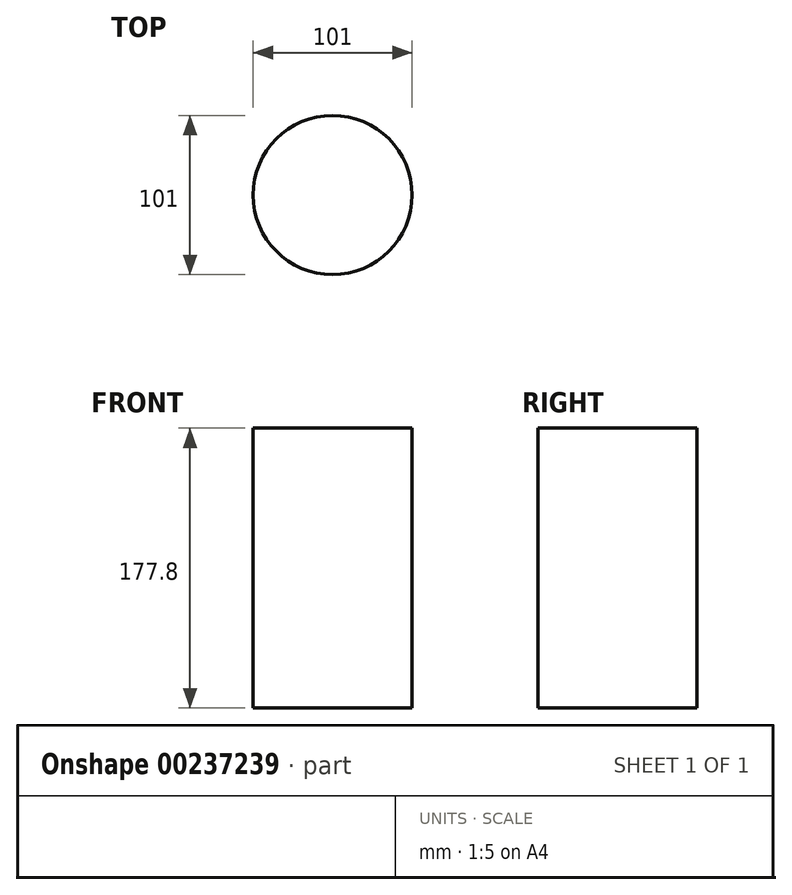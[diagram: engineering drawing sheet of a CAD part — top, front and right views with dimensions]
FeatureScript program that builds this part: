
annotation { "Feature Type Name" : "Feature", "Feature Type Description" : "" }
export const myFeature = defineFeature(function(context is Context, id is Id, definition is map)
    precondition{}
    {
        {
            var Q0;
            Q0=qCreatedBy(makeId("Top.planeOp"),FACE);
            var sketch = newSketch(context, id + "F0", { "sketchPlane" : qUnion([Q0])});
            skCircle(sketch, "E0", {"center": v(0, -7.12) * mm, "radius": 50.5 * mm});
            skSolve(sketch);
        }
        {
            var Q0;
            Q0=makeQuery(id+"F0.imprint","IMPRINT",FACE,{"disambiguationData":[TD([[makeQuery(id+"F0.imprint","IMPRINT",EDGE,{"derivedFrom":sQuery(id+"F0.wireOp",EDGE,"E0")}),1.0]])]});
            extrude(context, id + "F1", {"entities" : qUnion([Q0]), "depth" : 177.8 * mm});
        }
    });
